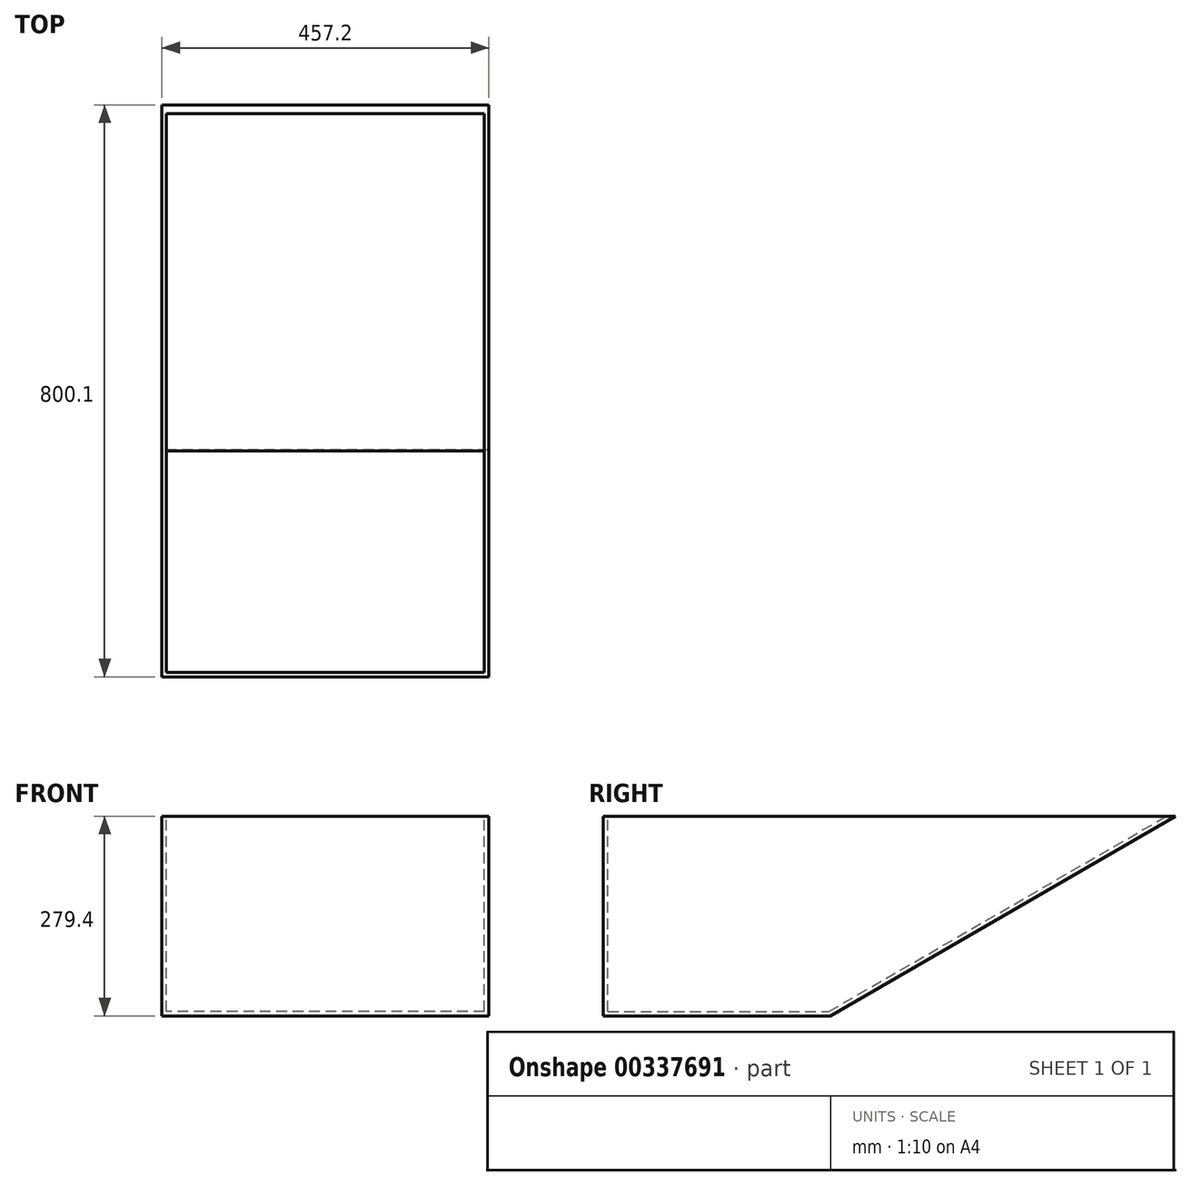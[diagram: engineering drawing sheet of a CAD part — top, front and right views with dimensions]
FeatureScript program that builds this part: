
annotation { "Feature Type Name" : "Feature", "Feature Type Description" : "" }
export const myFeature = defineFeature(function(context is Context, id is Id, definition is map)
    precondition{}
    {
        {
            var Q0;
            Q0=qCreatedBy(makeId("Right.planeOp"),FACE);
            var sketch = newSketch(context, id + "F0", { "sketchPlane" : qUnion([Q0])});
            skLineSegment(sketch, "E0", {"start": v(0, 0) * mm, "end": v(0, 279.4) * mm});
            skLineSegment(sketch, "E1", {"start": v(0, 279.4) * mm, "end": v(800.1, 279.4) * mm});
            skLineSegment(sketch, "E2", {"start": v(0, 0) * mm, "end": v(317.5, 0) * mm});
            skLineSegment(sketch, "E3", {"start": v(317.5, 0) * mm, "end": v(800.1, 279.4) * mm});
            skSolve(sketch);
        }
        {
            var Q0;
            Q0=makeQuery(id+"F0.imprint","IMPRINT",FACE,{"disambiguationData":[TD([[makeQuery(id+"F0.imprint","IMPRINT",EDGE,{"derivedFrom":sQuery(id+"F0.wireOp",EDGE,"E0")}),-1.0]])]});
            extrude(context, id + "F1", {"entities" : qUnion([Q0]), "depth" : 457.2 * mm});
        }
        {
            var Q0;
            Q0=makeQuery(id+"F1.opExtrude","SWEPT_FACE",FACE,{"disambiguationData":[OSD([sQuery(id+"F0.wireOp",EDGE,"E1")])]});
            shell(context, id + "F2", {"entities" : qUnion([Q0]), "thickness" : 6.35 * mm});
        }
    });
